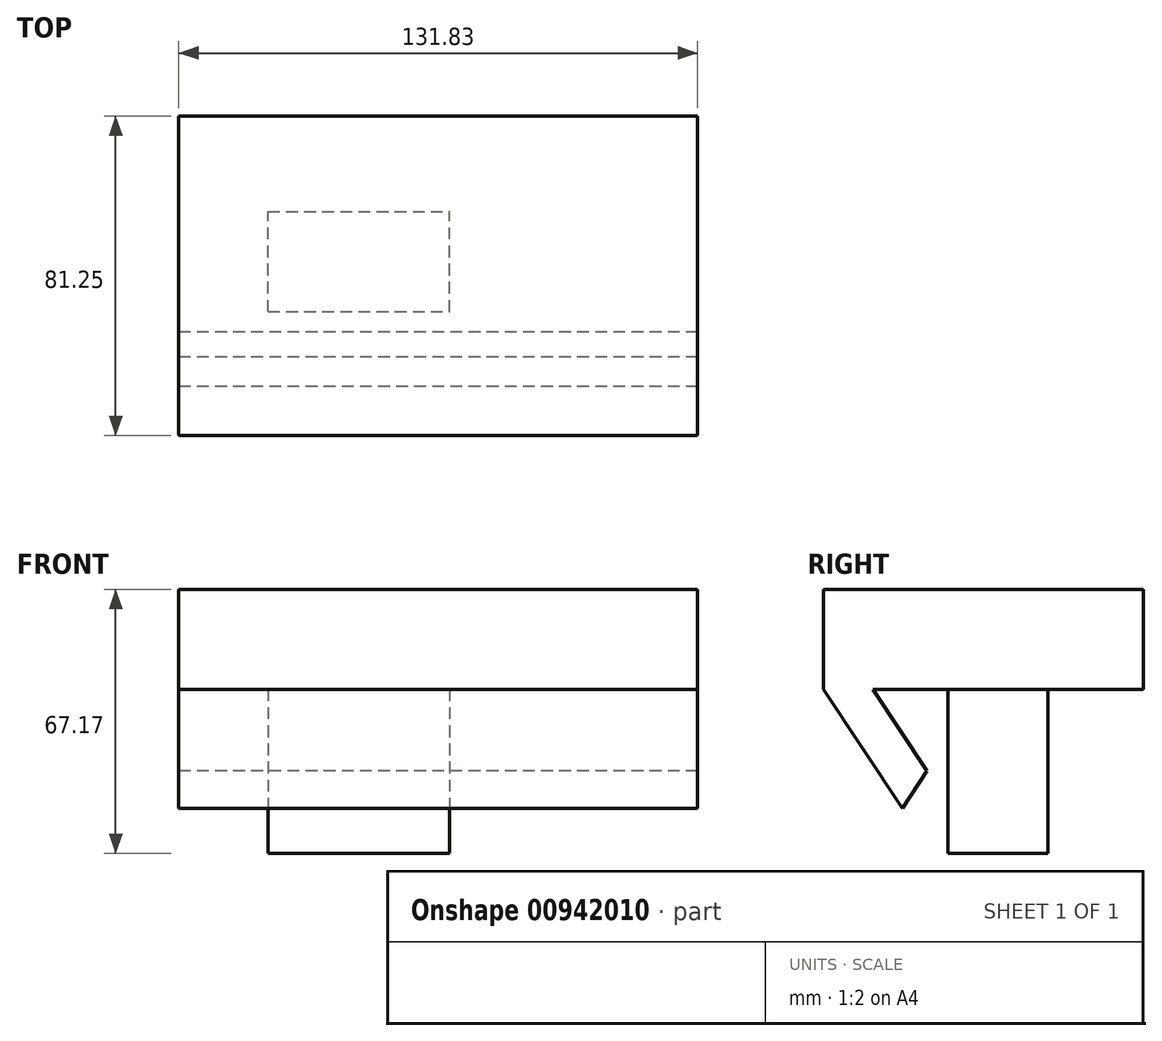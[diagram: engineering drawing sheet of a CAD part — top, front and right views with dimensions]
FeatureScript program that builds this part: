
annotation { "Feature Type Name" : "Feature", "Feature Type Description" : "" }
export const myFeature = defineFeature(function(context is Context, id is Id, definition is map)
    precondition{}
    {
        {
            var Q0;
            Q0=qCreatedBy(makeId("Front.planeOp"),FACE);
            var sketch = newSketch(context, id + "F0", { "sketchPlane" : qUnion([Q0])});
            skLineSegment(sketch, "E0.bottom", {"start": v(-105.26, -6.41) * mm, "end": v(-59.11, -6.41) * mm});
            skLineSegment(sketch, "E0.top", {"start": v(-105.26, -48.18) * mm, "end": v(-59.11, -48.18) * mm});
            skLineSegment(sketch, "E0.left", {"start": v(-105.26, -6.41) * mm, "end": v(-105.26, -48.18) * mm});
            skLineSegment(sketch, "E0.right", {"start": v(-59.11, -6.41) * mm, "end": v(-59.11, -48.18) * mm});
            skSolve(sketch);
        }
        {
            var Q0;
            Q0 = qSketchRegion(id + "F0", true);
            extrude(context, id + "F1", {"entities" : qUnion([Q0]), "depth" : 25.4 * mm, "offsetDistance" : 25.4 * mm});
        }
        {
            var Q0;
            Q0=makeQuery(id+"F1.opExtrude","SWEPT_FACE",FACE,{"disambiguationData":[OSD([sQuery(id+"F0.wireOp",EDGE,"E0.bottom")])]});
            var sketch = newSketch(context, id + "F2", { "sketchPlane" : qUnion([Q0])});
            skLineSegment(sketch, "E1.bottom", {"start": v(-127.91, 24.33) * mm, "end": v(3.92, 24.33) * mm});
            skLineSegment(sketch, "E1.top", {"start": v(-127.91, -56.92) * mm, "end": v(3.92, -56.92) * mm});
            skLineSegment(sketch, "E1.left", {"start": v(-127.91, 24.33) * mm, "end": v(-127.91, -56.92) * mm});
            skLineSegment(sketch, "E1.right", {"start": v(3.92, 24.33) * mm, "end": v(3.92, -56.92) * mm});
            skSolve(sketch);
        }
        {
            var Q0;
            Q0 = qSketchRegion(id + "F2", true);
            extrude(context, id + "F3", {"entities" : qUnion([Q0]), "depth" : 25.4 * mm, "offsetDistance" : 25.4 * mm});
        }
        {
            var Q0;
            Q0=makeQuery(id+"F3.opExtrude","SWEPT_FACE",FACE,{"disambiguationData":[OSD([sQuery(id+"F2.wireOp",EDGE,"E1.left")])]});
            var sketch = newSketch(context, id + "F4", { "sketchPlane" : qUnion([Q0])});
            skLineSegment(sketch, "E2", {"start": v(56.92, -6.41) * mm, "end": v(36.93, -36.64) * mm});
            skLineSegment(sketch, "E3", {"start": v(36.93, -36.64) * mm, "end": v(30.63, -27.17) * mm});
            skLineSegment(sketch, "E4", {"start": v(30.63, -27.17) * mm, "end": v(44.36, -6.41) * mm});
            skLineSegment(sketch, "E5", {"start": v(44.36, -6.41) * mm, "end": v(56.92, -6.41) * mm});
            skSolve(sketch);
        }
        {
            var Q0;
            Q0 = qSketchRegion(id + "F4", true);
            var Q1;
            Q1=makeQuery(id+"F3.opExtrude","SWEPT_FACE",FACE,{"disambiguationData":[OSD([sQuery(id+"F2.wireOp",EDGE,"E1.right")])]});
            extrude(context, id + "F5", {"entities" : qUnion([Q0]), "operationType" : NewBodyOperationType.ADD, "endBound" : BoundingType.UP_TO_SURFACE, "oppositeDirection" : true, "depth" : 132.6 * mm, "endBoundEntityFace" : qUnion([Q1]), "offsetDistance" : 25.4 * mm});
        }
    });
